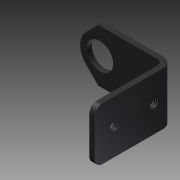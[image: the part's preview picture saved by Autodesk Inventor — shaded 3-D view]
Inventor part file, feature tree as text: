
AUTODESK INVENTOR PART (.ipt)
format: ipt  version: 2015 (Build 190159000, 159)  size: 245,760 bytes
history: native  units: mm
features: extrude x7, fillet x4, hole x3, chamfer x1, plane x1, other x1
ambient origin geometry x8: Origin, YZ Plane, XZ Plane, XY Plane, X Axis, Y Axis, Z Axis, Center Point
bodies: Solid1 (feature_tree)
feature tree (17):
  extrude  "Extrusión1"  Depth=2.0mm
  hole  "Agujero1"  [1 undecoded]
  hole  "Agujero2"  [1 undecoded]
  extrude  "Extrusión2"  Depth=2.0mm
  fillet  "Empalme1"  Radius=23.5mm
  chamfer  "Chaflán1"  Distance=22.1mm
  plane  "Plano de trabajo1"
  hole  "Agujero3"  [1 undecoded]
  extrude  "Extrusión5"  Depth=2.0mm TaperAngle=0.0deg
  fillet  "Empalme2"  Radius=4.0mm
  extrude  "Extrusión6"  Depth=4.0mm TaperAngle=45.0deg
  extrude  "Extrusión7"  Depth=2.0mm
  fillet  "Empalme3"  Radius=40.0mm
  extrude  "Extrusión8"  Depth=10.0mm TaperAngle=0.0deg
  extrude  "Extrusión10"  Depth=4.0mm
  fillet  "Redondeo de esquina1"  Radius=25.0mm
  other  "Definición1"
note: 3 required parameter values undecoded (feature->parameter linkage not recoverable at this tier; creation-order binding heuristic only, values carry confidence <= 0.55)
